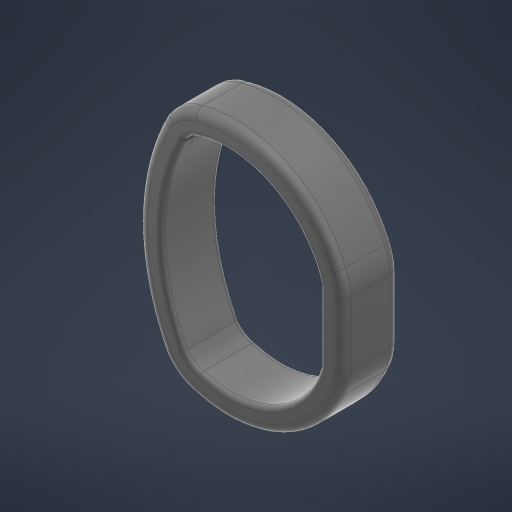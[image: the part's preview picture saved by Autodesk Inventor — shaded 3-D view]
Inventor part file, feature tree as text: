
AUTODESK INVENTOR PART (.ipt)
format: ipt  version: 2024 (Build 280153000, 153)  size: 479,744 bytes
history: native  units: in
note: dims shown in document units (in); Inventor stores cm internally (conversion verified against a paired STEP export)
features: fillet x3, extrude x1, sketch x1
ambient origin geometry x8: Origin, YZ Plane, XZ Plane, XY Plane, X Axis, Y Axis, Z Axis, Center Point
bodies: Solid1 (feature_tree)
feature tree (5):
  extrude  "Extrusion1"  Depth=0.0078in
  fillet  "Fillet1"  Radius=0.25in
  fillet  "Fillet2"  Radius=0.125in
  fillet  "Fillet3"  Radius=0.013in
  sketch  "Sketch1"  dims[d2=0.159in d3=0.1875in d7=0.25in d8=0.125in d9=0.013in d10=0.1681in d11=0.0625in d13=0.0375in d14=0.04in d15=0.04in d16=0.1in d17=0.0in d18=0.0156in d19=0.0078in d20=0.0078in d21=0.0in d22=0.0in]
